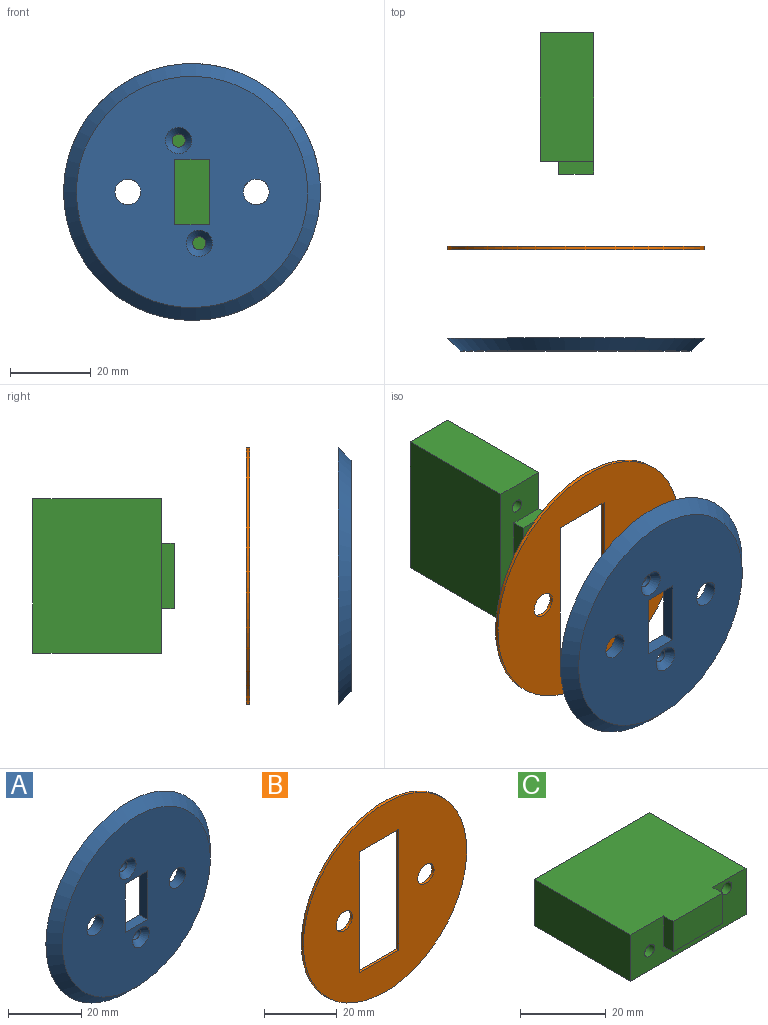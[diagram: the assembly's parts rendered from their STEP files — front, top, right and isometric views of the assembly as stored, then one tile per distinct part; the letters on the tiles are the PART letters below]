
ASSEMBLY  parts=3 mates=4
PART A: 13 faces, bbox 63.5x3.2x63.5 mm
  f0: plane 57.15x57.15mm, normal (0,-1,0), area 2295.6mm2, adj f2,f3,f4,f5,f7,f9,f10,f11
  f1: plane 63.5x63.5mm, normal (0,1,0), area 2946.5mm2, adj f2,f3,f4,f5,f6,f8,f10,f11
  f2: plane 16.26x3.18mm, normal (1,0,0), area 51.6mm2, adj f0,f1,f3,f5
  f3: plane 8.64x3.18mm, normal (0,0,1), area 27.4mm2, adj f0,f1,f2,f4
  f4: plane 16.26x3.18mm, normal (-1,0,0), area 51.6mm2, adj f0,f1,f3,f5
  f5: plane 8.64x3.18mm, normal (0,0,-1), area 27.4mm2, adj f0,f1,f2,f4
  f6: cylinder r=1.63mm len=3.26mm, axis (0,-1,0), area 13.6mm2, adj f1,f7
  f7: cone r=1.63mm half-angle=41deg, axis (0,-1,0), area 37.5mm2, adj f0,f6
  f8: cylinder r=1.63mm len=3.26mm, axis (0,-1,0), area 13.6mm2, adj f1,f9
  f9: cone r=1.63mm half-angle=41deg, axis (0,-1,0), area 37.5mm2, adj f0,f8
  f10: cylinder r=3.17mm len=6.35mm, axis (0,-1,0), area 63.3mm2, adj f0,f1
  f11: cylinder r=3.17mm len=6.35mm, axis (0,-1,0), area 63.3mm2, adj f0,f1
  f12: cone r=28.57mm half-angle=45deg, axis (0,1,0), area 851mm2, adj f0,f1
PART B: 9 faces, bbox 63.5x0.8x63.5 mm
  f0: plane 40.64x0.81mm, normal (-1,0,0), area 33mm2, adj f1,f3,f7,f8
  f1: plane 15.24x0.81mm, normal (0,0,1), area 12.4mm2, adj f0,f2,f7,f8
  f2: plane 40.64x0.81mm, normal (1,0,0), area 33mm2, adj f1,f3,f7,f8
  f3: plane 15.24x0.81mm, normal (0,0,-1), area 12.4mm2, adj f0,f2,f7,f8
  f4: cylinder r=3.17mm len=6.35mm, axis (0,1,0), area 16.2mm2, adj f7,f8
  f5: cylinder r=3.17mm len=6.35mm, axis (0,1,0), area 16.2mm2, adj f7,f8
  f6: cylinder r=31.75mm len=63.5mm, axis (0,1,0), area 162.1mm2, adj f7,f8
  f7: plane 63.5x63.5mm, normal (0,-1,0), area 2484.2mm2, adj f0,f1,f2,f3,f4,f5,f6
  f8: plane 63.5x63.5mm, normal (0,1,0), area 2484.2mm2, adj f0,f1,f2,f3,f4,f5,f6
PART C: 14 faces, bbox 38.1x34.9x13.2 mm
  f0: plane 38.1x13.21mm, normal (0,-1,0), area 346mm2, adj f1,f2,f3,f4,f6,f7,f8,f10
  f1: plane 38.1x31.75mm, normal (0,0,-1), area 1209.7mm2, adj f0,f2,f4,f5
  f2: plane 31.75x13.21mm, normal (1,0,0), area 419.4mm2, adj f0,f1,f3,f5
  f3: plane 38.1x34.93mm, normal (0,0,1), area 1261.3mm2, adj f0,f2,f4,f5,f7,f8,f9
  f4: plane 31.75x13.21mm, normal (-1,0,0), area 419.4mm2, adj f0,f1,f3,f5
  f5: plane 38.1x13.21mm, normal (0,1,0), area 503.2mm2, adj f1,f2,f3,f4
  f6: plane 16.26x3.18mm, normal (0,0,-1), area 51.6mm2, adj f0,f7,f8,f9
  f7: plane 8.64x3.18mm, normal (1,0,0), area 27.4mm2, adj f0,f3,f6,f9
  f8: plane 8.64x3.18mm, normal (-1,0,0), area 27.4mm2, adj f0,f3,f6,f9
  f9: plane 16.26x8.64mm, normal (0,-1,0), area 140.4mm2, adj f3,f6,f7,f8
  f10: cylinder r=1.64mm len=3.81mm, axis (0,-1,0), area 39.2mm2, adj f0,f11
  f11: plane 3.28x3.28mm, normal (0,-1,0), area 8.4mm2, adj f10
  f12: cylinder r=1.64mm len=3.81mm, axis (0,-1,0), area 39.2mm2, adj f0,f13
  f13: plane 3.28x3.28mm, normal (0,-1,0), area 8.4mm2, adj f12
PLACE A t=(0.08,14.22,0.12)mm fixed
PLACE B t=(0.08,36.9,0.12)mm
PLACE C rot(axis=(0,1,0),90deg) t=(-2.2,57.92,0.12)mm
MATE slider A.f10 <-> B.f5  axis (0,-1,0) through (15.96,12.64,0.12)mm
MATE planar C.f6 <-> A.f2  axis (-1,0,0) through (-4.23,57.92,0.12)mm
MATE planar C.f8 <-> A.f5  axis (0,0,1) through (0.08,56.33,8.25)mm
MATE slider A.f10 <-> B.f5  axis (0,-1,0) through (15.96,11.05,0.12)mm
